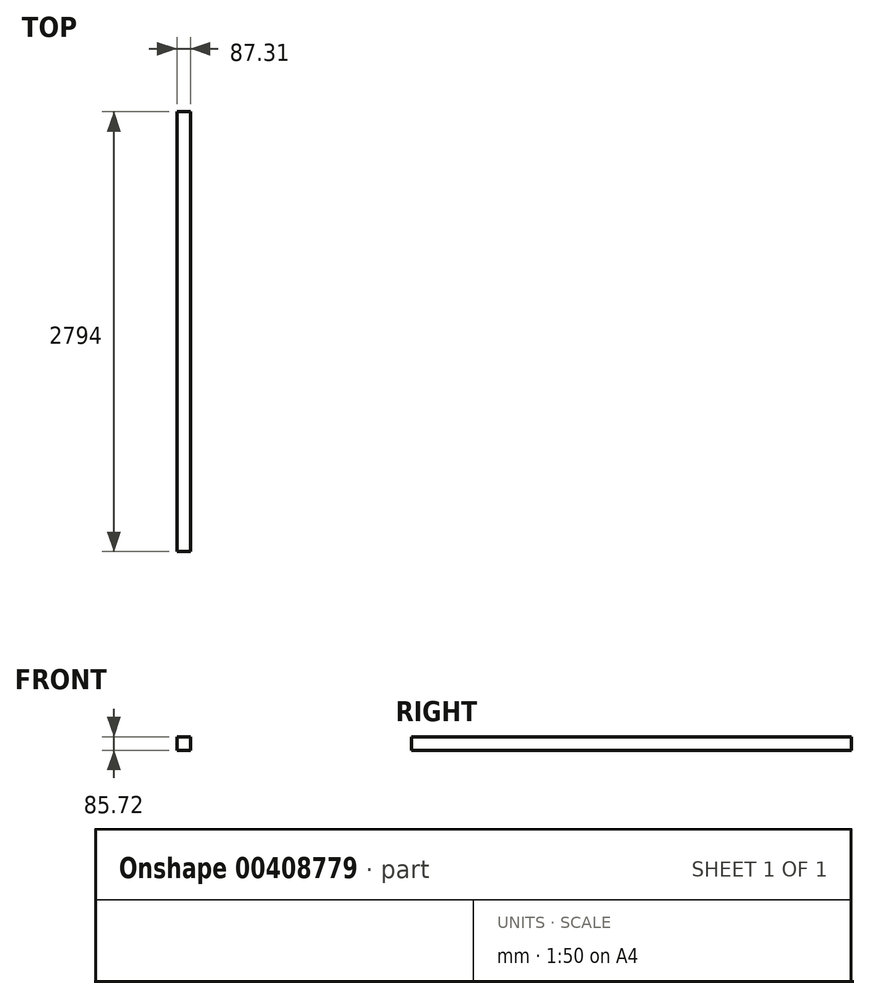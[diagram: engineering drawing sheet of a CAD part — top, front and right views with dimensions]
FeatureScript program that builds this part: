
annotation { "Feature Type Name" : "Feature", "Feature Type Description" : "" }
export const myFeature = defineFeature(function(context is Context, id is Id, definition is map)
    precondition{}
    {
        {
            var Q0;
            Q0=qCreatedBy(makeId("Front.planeOp"),FACE);
            var sketch = newSketch(context, id + "F0", { "sketchPlane" : qUnion([Q0])});
            skLineSegment(sketch, "E0.bottom", {"start": v(0, 0) * mm, "end": v(-87.31, 0) * mm});
            skLineSegment(sketch, "E0.top", {"start": v(0, 85.73) * mm, "end": v(-87.31, 85.73) * mm});
            skLineSegment(sketch, "E0.left", {"start": v(0, 0) * mm, "end": v(0, 85.72) * mm});
            skLineSegment(sketch, "E0.right", {"start": v(-87.31, 0) * mm, "end": v(-87.31, 85.72) * mm});
            skSolve(sketch);
        }
        {
            var Q0;
            Q0 = qSketchRegion(id + "F0", true);
            extrude(context, id + "F1", {"entities" : qUnion([Q0]), "depth" : 2794 * mm});
        }
    });
